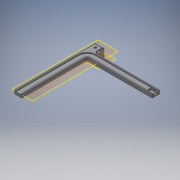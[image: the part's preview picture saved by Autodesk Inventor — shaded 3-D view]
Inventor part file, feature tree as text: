
AUTODESK INVENTOR PART (.ipt)
format: ipt  version: 2017 (Build 210142000, 142)  size: 251,392 bytes
history: native  units: mm
features: projected_geometry x8, sketch x7, extrude x5, fillet x4, plane x2, sweep x1
ambient origin geometry x8: Origin, YZ Plane, XZ Plane, XY Plane, X Axis, Y Axis, Z Axis, Center Point
bodies: Solid1 (feature_tree)
feature tree (27):
  extrude  "Extrusion1"  Depth=10.0mm
  extrude  "Extrusion2"  Depth=7.0mm
  fillet  "Fillet1"  Radius=7.0mm
  plane  "Work Plane1"
  sweep  "Sweep1"
  extrude  "Extrusion5"  Depth=20.0mm
  fillet  "Fillet2"  Radius=135.0mm
  fillet  "Fillet3"  Radius=5.0mm
  fillet  "Fillet4"  Radius=10.6mm
  extrude  "Extrusion6"  Depth=2.0mm
  plane  "Work Plane2"
  extrude  "Extrusion7"  Depth=5.0mm
  sketch  "Sketch1"  dims[d0=10.0mm d1=13.0mm]
  sketch  "Sketch2"  dims[d2=7.0mm d3=7.0mm d5=7.0mm]
  projected_geometry  "Projected Loop1"
  sketch  "Sketch6"  dims[d6=170.0mm d7=15.0mm d8=0.0mm]
  projected_geometry  "Projected Loop5"
  sketch  "Sketch7"  dims[d9=15.0mm d10=20.0mm d11=135.0mm d12=0.0mm d13=5.0mm d23=10.6mm]
  projected_geometry  "Projected Loop6"
  sketch  "Sketch8"  dims[d24=2.0mm d25=7.5mm]
  projected_geometry  "Projected Loop7"
  projected_geometry  "Projected Loop8"
  projected_geometry  "Projected Loop9"
  sketch  "Sketch9"  dims[d26=0.0mm d27=0.0mm d29=5.0mm]
  sketch  "Sketch10"  dims[d30=5.0mm d31=15.0mm d32=5.0mm d33=5.75mm d34=0.0mm d35=4.0mm d36=2.0mm d37=2.0mm d38=4.35mm d39=6.314168mm d40=10.0mm d41=0.0mm d42=7.25mm d43=4.0mm d44=0.0mm]
  projected_geometry  "Projected Loop10"
  projected_geometry  "Projected Loop11"
